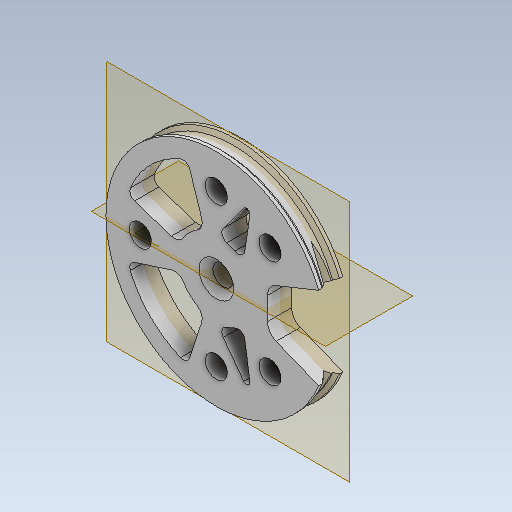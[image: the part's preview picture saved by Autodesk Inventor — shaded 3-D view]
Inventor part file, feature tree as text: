
AUTODESK INVENTOR PART (.ipt)
format: ipt  version: 2023 (Build 270158000, 158)  size: 460,800 bytes
history: native  units: mm
features: sketch x17, extrude x15, projected_geometry x14, other x7, fillet x5, plane x4, reference x4, revolve x2, chamfer x1, mirror x1
ambient origin geometry x8: Origin, YZ Plane, XZ Plane, XY Plane, X Axis, Y Axis, Z Axis, Center Point
bodies: Solid1 (feature_tree)
feature tree (70):
  extrude  "Extrusion1"  Depth=3.5mm TaperAngle=0.0deg
  sketch  "Sketch2"  dims[d3=8.0mm d4=3.5mm d5=0.0mm]
  plane  "Work Plane1"
  extrude  "Extrusion2"  Depth=3.5mm TaperAngle=0.0deg
  extrude  "Extrusion3"  Depth=20.0mm TaperAngle=0.0deg
  plane  "Work Plane2"
  extrude  "Extrusion4"  Depth=10.0mm
  plane  "Work Plane3"
  revolve  "Revolution1"  [1 undecoded]
  extrude  "Extrusion5"  Depth=0.5mm
  extrude  "Extrusion6"  Depth=0.5mm
  fillet  "Fillet1"  Radius=20.0mm
  extrude  "Extrusion7"  TaperAngle=45.0deg  [1 undecoded]
  extrude  "Extrusion8"  Depth=11.0mm
  extrude  "Extrusion9"  Depth=11.0mm
  extrude  "Extrusion10"  Depth=20.0mm TaperAngle=0.0deg
  extrude  "Extrusion11"  Depth=3.839724mm
  extrude  "Extrusion12"  Depth=2.0mm
  fillet  "Fillet2"  Radius=0.7mm
  chamfer  "Chamfer1"  Distance=20.0mm
  extrude  "Extrusion13"  Depth=20.0mm TaperAngle=0.0deg
  fillet  "Fillet3"  Radius=11.0mm
  fillet  "Fillet4"  Radius=3.2mm
  plane  "Work Plane4"
  mirror  "Mirror1"
  fillet  "Fillet5"  Radius=11.0mm
  revolve  "Revolution2"  [1 undecoded]
  extrude  "Extrusion14"  Depth=11.0mm
  extrude  "Extrusion15"  Depth=10.0mm TaperAngle=0.0deg
  sketch  "Sketch1"  dims[d0=32.0mm d1=3.5mm d2=0.0mm]
  reference  "Reference1"
  reference  "Reference2"
  reference  "Reference3"
  reference  "Reference4"
  sketch  "Sketch3"  dims[d6=3.0mm d7=20.0mm d8=0.0mm]
  projected_geometry  "Projected Loop1"
  sketch  "Sketch4"  dims[d9=10.0mm d10=3.0mm]
  projected_geometry  "Projected Loop2"
  sketch  "Sketch5"  dims[d11=3.0mm d12=20.0mm d13=0.0mm]
  projected_geometry  "Projected Loop3"
  projected_geometry  "Projected Loop4"
  sketch  "Sketch6"  dims[d14=1.5mm d15=0.5mm]
  projected_geometry  "Projected Loop5"
  sketch  "Sketch7"  dims[d16=0.5mm d17=0.5mm d18=20.0mm]
  projected_geometry  "Projected Loop6"
  sketch  "Sketch8"  dims[d19=90.0deg d20=45.0deg]
  projected_geometry  "Projected Loop7"
  sketch  "Sketch9"  dims[d21=45.0deg d22=11.0mm]
  projected_geometry  "Projected Loop8"
  sketch  "Sketch10"  dims[d23=3.2mm d24=11.0mm]
  sketch  "Sketch11"  dims[d25=3.2mm d26=20.0mm d27=0.0mm]
  projected_geometry  "Projected Loop9"
  sketch  "Sketch12"  dims[d28=3.839724mm d29=3.839724mm]
  projected_geometry  "Projected Loop10"
  sketch  "Sketch13"  dims[d30=20.0mm d31=0.0mm d32=2.0mm d33=0.7mm d34=20.0mm d35=0.0mm]
  projected_geometry  "Projected Loop11"
  sketch  "Sketch14"  dims[d36=0.7mm d37=20.0mm d38=0.0mm d41=11.0mm d42=3.2mm d43=11.0mm]
  projected_geometry  "Projected Loop12"
  sketch  "Sketch15"  dims[d44=3.2mm d45=20.0mm d46=0.0mm]
  sketch  "Sketch16"  dims[d47=20.0mm d48=0.0mm d49=11.0mm]
  projected_geometry  "Projected Loop13"
  sketch  "Sketch17"  dims[d50=3.2mm d51=20.0mm d52=0.0mm d53=27.0mm d54=11.0mm d55=3.141593mm d56=3.141593mm d57=3.141593mm d58=3.141593mm d59=20.0mm d60=0.0mm d61=1.5mm d62=1.0mm d63=1.0mm d64=2.0mm d65=45.0deg d66=11.0mm d67=13.5mm d68=20.0mm d69=0.0mm d70=0.5mm d71=1.0mm d72=1.5mm d76=0.5mm d77=0.5mm d78=5.0mm d79=360.0deg d80=10.0mm d81=0.0mm d82=10.0mm d83=0.0mm]
  projected_geometry  "Projected Loop14"
  parser-record x1  (decoder bookkeeping rows leaked as tree rows — omitted from the tree; the rows remain in map.json)
  other  "reducer_1.iam"
  other  "bearing_3_6_2:1"
  other  "tendon_wh_1:1"
  other  "mot_holder_1:1"
  other  "mot_27_ass:1"
  other  "mot_27_1:1"
note: 3 required parameter values undecoded (feature->parameter linkage not recoverable at this tier; creation-order binding heuristic only, values carry confidence <= 0.55)
note: 1 file-system path scrubbed to <path> (originals preserved in map.json)